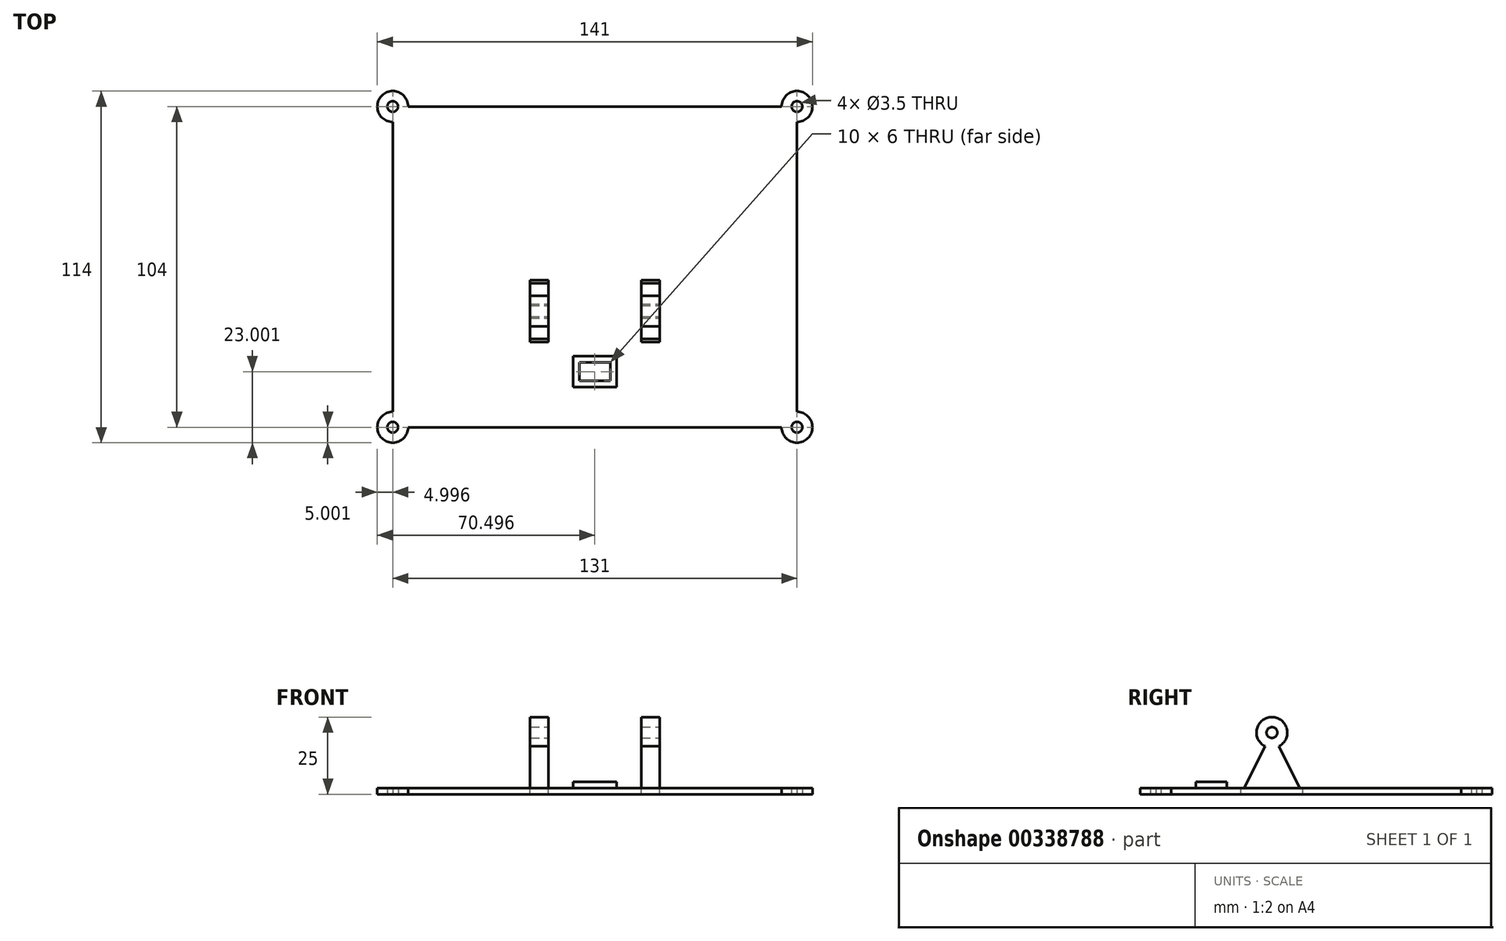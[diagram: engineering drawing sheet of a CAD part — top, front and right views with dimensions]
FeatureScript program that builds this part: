
annotation { "Feature Type Name" : "Feature", "Feature Type Description" : "" }
export const myFeature = defineFeature(function(context is Context, id is Id, definition is map)
    precondition{}
    {
        {
            var Q0;
            Q0=qCreatedBy(makeId("Top.planeOp"),FACE);
            var sketch = newSketch(context, id + "F0", { "sketchPlane" : qUnion([Q0])});
            skArc(sketch, "E0", {"start": v(-87.85, 71.33) * mm, "mid": v(-92.84, 66.33) * mm, "end": v(-87.84, 61.33) * mm});
            skLineSegment(sketch, "E1", {"start": v(-82.84, 66.33) * mm, "end": v(-82.84, 66.33) * mm});
            skArc(sketch, "E2", {"start": v(-87.84, -32.67) * mm, "mid": v(-91.38, -41.2) * mm, "end": v(-82.84, -37.67) * mm});
            skLineSegment(sketch, "E3", {"start": v(-82.84, -37.67) * mm, "end": v(-82.84, -37.67) * mm});
            skLineSegment(sketch, "E4", {"start": v(-82.84, -37.67) * mm, "end": v(-22.34, -37.67) * mm});
            skArc(sketch, "E5", {"start": v(-82.84, 66.33) * mm, "mid": v(-84.3, 69.87) * mm, "end": v(-87.85, 71.33) * mm});
            skLineSegment(sketch, "E6", {"start": v(43.16, 61.33) * mm, "end": v(43.16, 61.33) * mm});
            skArc(sketch, "E7", {"start": v(43.16, 61.33) * mm, "mid": v(46.7, 69.87) * mm, "end": v(38.16, 66.33) * mm});
            skArc(sketch, "E8", {"start": v(38.16, -37.67) * mm, "mid": v(46.7, -41.2) * mm, "end": v(43.16, -32.67) * mm});
            skCircle(sketch, "E9", {"center": v(-87.84, 66.33) * mm, "radius": 1.75 * mm});
            skCircle(sketch, "E10", {"center": v(43.16, 66.33) * mm, "radius": 1.75 * mm});
            skCircle(sketch, "E11", {"center": v(-87.84, -37.67) * mm, "radius": 1.75 * mm});
            skCircle(sketch, "E12", {"center": v(43.16, -37.67) * mm, "radius": 1.75 * mm});
            skLineSegment(sketch, "E13", {"start": v(-22.34, -37.67) * mm, "end": v(38.16, -37.67) * mm});
            skLineSegment(sketch, "E14.bottom", {"start": v(-27.34, -16.67) * mm, "end": v(-17.34, -16.67) * mm});
            skLineSegment(sketch, "E14.left", {"start": v(-27.34, -16.67) * mm, "end": v(-27.34, -22.67) * mm});
            skLineSegment(sketch, "E14.right", {"start": v(-17.34, -16.67) * mm, "end": v(-17.34, -22.67) * mm});
            skLineSegment(sketch, "E15", {"start": v(-87.84, 61.33) * mm, "end": v(-87.84, -32.67) * mm});
            skLineSegment(sketch, "E16", {"start": v(-82.84, 66.33) * mm, "end": v(38.16, 66.33) * mm});
            skLineSegment(sketch, "E17", {"start": v(43.16, 61.33) * mm, "end": v(43.16, -32.67) * mm});
            skLineSegment(sketch, "E18", {"start": v(-29.34, -14.67) * mm, "end": v(-15.34, -14.67) * mm});
            skLineSegment(sketch, "E19", {"start": v(-15.34, -14.67) * mm, "end": v(-15.34, -24.67) * mm});
            skLineSegment(sketch, "E20", {"start": v(-15.34, -24.67) * mm, "end": v(-29.34, -24.67) * mm});
            skLineSegment(sketch, "E21", {"start": v(-29.34, -24.67) * mm, "end": v(-29.34, -14.67) * mm});
            skLineSegment(sketch, "E22", {"start": v(-27.34, -22.67) * mm, "end": v(-17.34, -22.67) * mm});
            skSolve(sketch);
        }
        {
            var Q0;
            Q0=qCreatedBy(makeId("Front.planeOp"),FACE);
            var sketch = newSketch(context, id + "F1", { "sketchPlane" : qUnion([Q0])});
            skLineSegment(sketch, "E23", {"start": v(-43.34, 0) * mm, "end": v(-37.34, 0) * mm});
            skLineSegment(sketch, "E24", {"start": v(-7.34, 0) * mm, "end": v(-1.34, 0) * mm});
            skLineSegment(sketch, "E25.top", {"start": v(-43.34, 25) * mm, "end": v(-37.34, 25) * mm});
            skLineSegment(sketch, "E25.left", {"start": v(-43.34, 0) * mm, "end": v(-43.34, 25) * mm});
            skLineSegment(sketch, "E25.right", {"start": v(-37.34, 0) * mm, "end": v(-37.34, 25) * mm});
            skLineSegment(sketch, "E26.top", {"start": v(-7.34, 25) * mm, "end": v(-1.34, 25) * mm});
            skLineSegment(sketch, "E26.left", {"start": v(-7.34, 0) * mm, "end": v(-7.34, 25) * mm});
            skLineSegment(sketch, "E26.right", {"start": v(-1.34, 0) * mm, "end": v(-1.34, 25) * mm});
            skPoint(sketch, "E27.0", {"position": v(0, 0) * mm});
            skSolve(sketch);
        }
        {
            var Q0;
            Q0=makeQuery(id+"F1.imprint","IMPRINT",FACE,{"disambiguationData":[TD([[makeQuery(id+"F1.imprint","IMPRINT",EDGE,{"derivedFrom":sQuery(id+"F1.wireOp",EDGE,"E23")}),1.0]])]});
            var Q1;
            Q1=makeQuery(id+"F1.imprint","IMPRINT",FACE,{"disambiguationData":[TD([[makeQuery(id+"F1.imprint","IMPRINT",EDGE,{"derivedFrom":sQuery(id+"F1.wireOp",EDGE,"E24")}),1.0]])]});
            extrude(context, id + "F2", {"entities" : qUnion([Q0, Q1]), "endBound" : BoundingType.SYMMETRIC, "depth" : 20 * mm});
        }
        {
            var Q0;
            Q0 = qSketchRegion(id + "F0", true);
            extrude(context, id + "F3", {"entities" : qUnion([Q0]), "depth" : 2 * mm});
        }
        {
            var Q0;
            Q0=qCreatedBy(makeId("Right.planeOp"),FACE);
            var sketch = newSketch(context, id + "F4", { "sketchPlane" : qUnion([Q0])});
            skLineSegment(sketch, "E28.0.0", {"start": v(10, 0) * mm, "end": v(10, 2.02) * mm});
            skLineSegment(sketch, "E28.0.1", {"start": v(10, 25) * mm, "end": v(0, 25) * mm});
            skLineSegment(sketch, "E28.0.2", {"start": v(-10, 25) * mm, "end": v(-10, 2.02) * mm});
            skLineSegment(sketch, "E28.0.3", {"start": v(-10, 0) * mm, "end": v(10, 0) * mm});
            skLineSegment(sketch, "E29", {"start": v(0, 25) * mm, "end": v(-10, 25) * mm});
            skCircle(sketch, "E30", {"center": v(0, 20) * mm, "radius": 5 * mm});
            skPoint(sketch, "E30.second.point", {"position": v(0, 15) * mm});
            skPoint(sketch, "E30.third.point", {"position": v(-2.77, 15.83) * mm});
            skLineSegment(sketch, "E31", {"start": v(0, 20) * mm, "end": v(10, 0) * mm});
            skLineSegment(sketch, "E32", {"start": v(0, 20) * mm, "end": v(-10, 0) * mm});
            skCircle(sketch, "E33", {"center": v(0, 20) * mm, "radius": 1.75 * mm});
            skLineSegment(sketch, "E34", {"start": v(10, 2.02) * mm, "end": v(10, 25) * mm});
            skLineSegment(sketch, "E35", {"start": v(-10, 2.02) * mm, "end": v(-10, 0) * mm});
            skLineSegment(sketch, "E36", {"start": v(10, 2.02) * mm, "end": v(-10, 2.02) * mm});
            skSolve(sketch);
        }
        {
            var Q0;
            {var subQ2=sQuery(id+"F4.wireOp",EDGE,"E28.0.1");Q0=makeQuery(id+"F4.imprint","IMPRINT",FACE,{"disambiguationData":[TD([[makeQuery(id+"F4.imprint","IMPRINT",EDGE,{"derivedFrom":subQ2}),1.0]])]});}
            var Q1;
            {var subQ6=sQuery(id+"F4.wireOp",EDGE,"E28.0.2");Q1=makeQuery(id+"F4.imprint","IMPRINT",FACE,{"disambiguationData":[TD([[makeQuery(id+"F4.imprint","IMPRINT",EDGE,{"derivedFrom":subQ6}),1.0]])]});}
            var Q2;
            {var subQ0=sQuery(id+"F4.wireOp",EDGE,"E32");var subQ1=sQuery(id+"F4.wireOp",EDGE,"E31");var subQ2=makeQuery(id+"F4.imprint","INTERSECT",VERTEX,{"derivedFrom":[subQ1,subQ0]});Q2=makeQuery(id+"F4.imprint","IMPRINT",FACE,{"disambiguationData":[TD([[makeQuery(id+"F4.imprint","IMPRINT",EDGE,{"disambiguationData":[TD([[subQ2,-1.0]])],"derivedFrom":subQ1}),1.0]])]});}
            var Q3;
            {var subQ0=sQuery(id+"F4.wireOp",EDGE,"E32");var subQ1=sQuery(id+"F4.wireOp",EDGE,"E31");var subQ2=makeQuery(id+"F4.imprint","INTERSECT",VERTEX,{"derivedFrom":[subQ1,subQ0]});Q3=makeQuery(id+"F4.imprint","IMPRINT",FACE,{"disambiguationData":[TD([[makeQuery(id+"F4.imprint","IMPRINT",EDGE,{"disambiguationData":[TD([[subQ2,-1.0]])],"derivedFrom":subQ1}),-1.0]])]});}
            extrude(context, id + "F5", {"entities" : qUnion([Q0, Q1, Q2, Q3]), "operationType" : NewBodyOperationType.REMOVE, "endBound" : BoundingType.THROUGH_ALL, "oppositeDirection" : true, "depth" : 25 * mm});
        }
        {
            var Q0;
            Q0=makeQuery(id+"F0.imprint","IMPRINT",FACE,{"disambiguationData":[TD([[makeQuery(id+"F0.imprint","IMPRINT",EDGE,{"derivedFrom":sQuery(id+"F0.wireOp",EDGE,"E14.bottom")}),1.0]])]});
            extrude(context, id + "F6", {"entities" : qUnion([Q0]), "operationType" : NewBodyOperationType.ADD, "depth" : 4 * mm});
        }
    });
